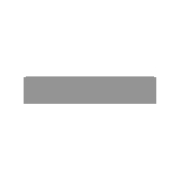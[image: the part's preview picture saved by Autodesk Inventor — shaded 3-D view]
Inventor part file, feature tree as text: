
AUTODESK INVENTOR PART (.ipt)
format: ipt  version: 2019 (Build 230136000, 136)  size: 108,544 bytes
history: native  units: mm
features: other x6, sketch x3, extrude x1
ambient origin geometry x8: Origin, YZ Plane, XZ Plane, XY Plane, X Axis, Y Axis, Z Axis, Center Point
bodies: Body1 (feature_tree)
feature tree (10):
  other  "Контрольная длина"
  other  "Генератор рам"
  other  "Твердое тело1"
  other  "Начальная плоскость"
  other  "Конечная плоскость"
  extrude  "Тело"  TaperAngle=0.0deg  [1 undecoded]
  sketch  "Эскиз"
  sketch  "Эскиз6"
  other  "РабПлоскость5"
  sketch  "Эскиз7"
note: 1 required parameter value undecoded (feature->parameter linkage not recoverable at this tier; creation-order binding heuristic only, values carry confidence <= 0.55)
